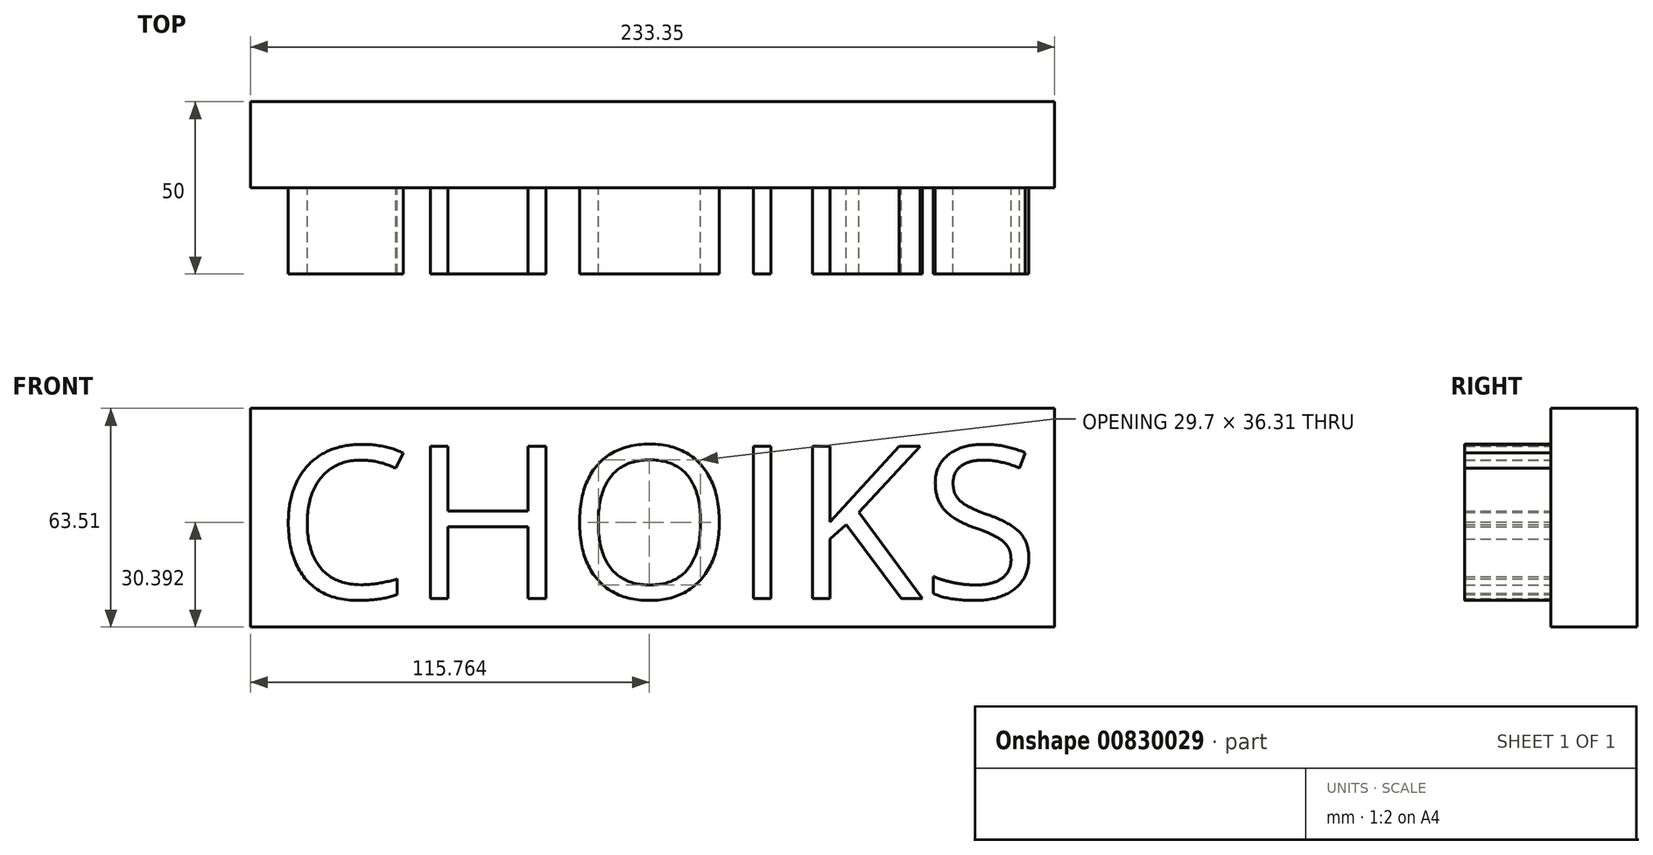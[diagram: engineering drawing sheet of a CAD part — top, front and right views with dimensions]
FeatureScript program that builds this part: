
annotation { "Feature Type Name" : "Feature", "Feature Type Description" : "" }
export const myFeature = defineFeature(function(context is Context, id is Id, definition is map)
    precondition{}
    {
        {
            var Q0;
            Q0=qCreatedBy(makeId("Front.planeOp"),FACE);
            var sketch = newSketch(context, id + "F0", { "sketchPlane" : qUnion([Q0])});
            skText(sketch, "E0", { "text": "CHOIKS\n", "fontName": "OpenSans-Regular.ttf"});
            const initialGuessF0  = {"E0": [-0.08537, -0.0293, 1, 0, 0.04446]};
            skSetInitialGuess(sketch, initialGuessF0);
            skSolve(sketch);
        }
        {
            var Q0;
            Q0 = qSketchRegion(id + "F0", true);
            extrude(context, id + "F1", {"entities" : qUnion([Q0]), "depth" : 25 * mm, "offsetDistance" : 25 * mm});
        }
        {
            var Q0;
            Q0=makeQuery(id+"F1.opExtrude","CAP_FACE",FACE,{"disambiguationData":[OSD([sQuery(id+"F0.wireOp",EDGE,"E0.sketch_text.stroke-27"),sQuery(id+"F0.wireOp",EDGE,"E0.sketch_text.stroke-28"),sQuery(id+"F0.wireOp",EDGE,"E0.sketch_text.stroke-29"),sQuery(id+"F0.wireOp",EDGE,"E0.sketch_text.stroke-30"),sQuery(id+"F0.wireOp",EDGE,"E0.sketch_text.stroke-31"),sQuery(id+"F0.wireOp",EDGE,"E0.sketch_text.stroke-32"),sQuery(id+"F0.wireOp",EDGE,"E0.sketch_text.stroke-33"),sQuery(id+"F0.wireOp",EDGE,"E0.sketch_text.stroke-34"),sQuery(id+"F0.wireOp",EDGE,"E0.sketch_text.stroke-35"),sQuery(id+"F0.wireOp",EDGE,"E0.sketch_text.stroke-36"),sQuery(id+"F0.wireOp",EDGE,"E0.sketch_text.stroke-37"),sQuery(id+"F0.wireOp",EDGE,"E0.sketch_text.stroke-38"),sQuery(id+"F0.wireOp",EDGE,"E0.sketch_text.stroke-39"),sQuery(id+"F0.wireOp",EDGE,"E0.sketch_text.stroke-40"),sQuery(id+"F0.wireOp",EDGE,"E0.sketch_text.stroke-41"),sQuery(id+"F0.wireOp",EDGE,"E0.sketch_text.stroke-42")])],"isStart":true});
            var sketch = newSketch(context, id + "F2", { "sketchPlane" : qUnion([Q0])});
            skLineSegment(sketch, "E1.bottom", {"start": v(-140.78, 25.86) * mm, "end": v(92.57, 25.86) * mm});
            skLineSegment(sketch, "E1.top", {"start": v(-140.78, -37.65) * mm, "end": v(92.57, -37.65) * mm});
            skLineSegment(sketch, "E1.left", {"start": v(-140.78, 25.86) * mm, "end": v(-140.78, -37.65) * mm});
            skLineSegment(sketch, "E1.right", {"start": v(92.57, 25.86) * mm, "end": v(92.57, -37.65) * mm});
            skSolve(sketch);
        }
        {
            var Q0;
            Q0 = qSketchRegion(id + "F2", true);
            extrude(context, id + "F3", {"entities" : qUnion([Q0]), "depth" : 25 * mm, "offsetDistance" : 25 * mm});
        }
    });
